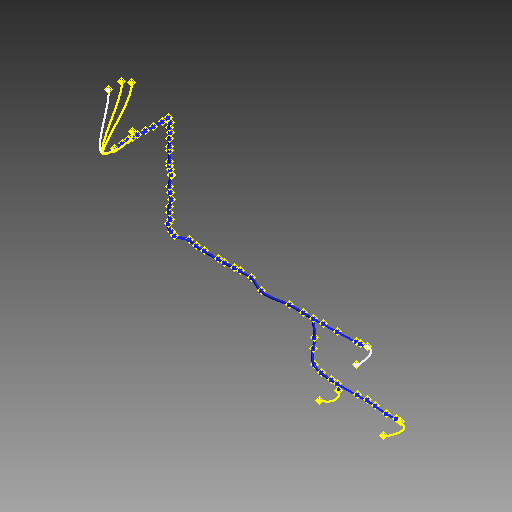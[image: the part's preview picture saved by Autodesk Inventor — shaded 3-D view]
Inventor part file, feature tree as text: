
AUTODESK INVENTOR PART (.ipt)
format: ipt  version: 2017 (Build 210142000, 142)  size: 543,232 bytes
history: native  units: mm (DEFAULTED — no unit token found)
features: other x85, plane x7, sketch x7, sweep x7
ambient origin geometry x8: Origin, YZ Plane, XZ Plane, XY Plane, X Axis, Y Axis, Z Axis, Center Point
bodies: Body1 (feature_tree), Body2 (feature_tree), Body3 (feature_tree), Body4 (feature_tree), Body5 (feature_tree), Body6 (feature_tree), Body7 (feature_tree)
feature tree (106):
  other  "Work Point1"
  other  "Work Point2"
  other  "Wire1"
  other  "Work Point3"
  other  "Work Point4"
  other  "Wire2"
  other  "Work Point5"
  other  "Work Point6"
  other  "Wire3"
  other  "Work Point7"
  other  "Work Point8"
  other  "Wire4"
  other  "Work Point9"
  other  "Work Point10"
  other  "Segment1"
  other  "Work Point11"
  other  "Work Point12"
  other  "Work Point13"
  other  "Work Point14"
  other  "Work Point15"
  other  "Work Point16"
  other  "Work Point17"
  other  "Work Point18"
  other  "Work Point19"
  other  "Work Point20"
  other  "Work Point21"
  other  "Work Point22"
  other  "Work Point23"
  other  "Work Point24"
  other  "Work Point25"
  other  "Work Point26"
  other  "Work Point27"
  other  "Work Point28"
  other  "Work Point29"
  other  "Segment2"
  other  "Work Point30"
  other  "Work Point31"
  other  "Work Point32"
  other  "Segment3"
  other  "Work Point33"
  other  "Work Point34"
  other  "Work Point35"
  other  "Work Point36"
  other  "Work Point37"
  other  "Work Point38"
  other  "Work Point39"
  other  "Work Point40"
  other  "Work Point41"
  other  "Work Point42"
  other  "Work Point43"
  other  "Work Point44"
  other  "Work Point45"
  other  "Work Point46"
  other  "Work Point47"
  other  "Work Point48"
  other  "Work Point49"
  other  "Work Point50"
  other  "Work Point51"
  other  "Work Point52"
  other  "Work Point53"
  other  "Work Point54"
  other  "Segment4"
  plane  "Work Plane2"
  plane  "Work Plane3"
  other  "Work Point55"
  other  "Segment5"
  other  "Work Point56"
  other  "Work Point57"
  other  "Work Point58"
  other  "Work Point59"
  other  "Work Point60"
  other  "Work Point61"
  other  "Segment6"
  plane  "Work Plane5"
  plane  "Work Plane6"
  other  "Work Point62"
  other  "Segment7"
  other  "Work Point63"
  other  "Work Point64"
  other  "Work Point65"
  other  "Work Point66"
  other  "Work Point67"
  plane  "Work Plane7"
  plane  "Work Plane8"
  plane  "Work Plane9"
  sketch  "Sketch2"  dims[d2=0.0mm d3=0.0mm d4=0.0mm d5=0.0mm]
  other  "Srf2"
  sketch  "Sketch3"  dims[d8=0.0mm d9=0.0mm d10=0.0mm d11=0.0mm]
  other  "Srf3"
  sketch  "Sketch5"  dims[d12=0.0mm d13=0.0mm d14=0.0mm d15=0.0mm]
  other  "Srf5"
  sketch  "Sketch6"  dims[d16=0.0mm d17=0.0mm]
  other  "Srf6"
  sketch  "Sketch7"
  other  "Srf7"
  sketch  "Sketch8"
  other  "Srf8"
  sketch  "Sketch9"
  other  "Srf9"
  sweep  "SweepSrf2"
  sweep  "SweepSrf3"
  sweep  "SweepSrf5"
  sweep  "SweepSrf6"
  sweep  "SweepSrf7"
  sweep  "SweepSrf8"
  sweep  "SweepSrf9"
